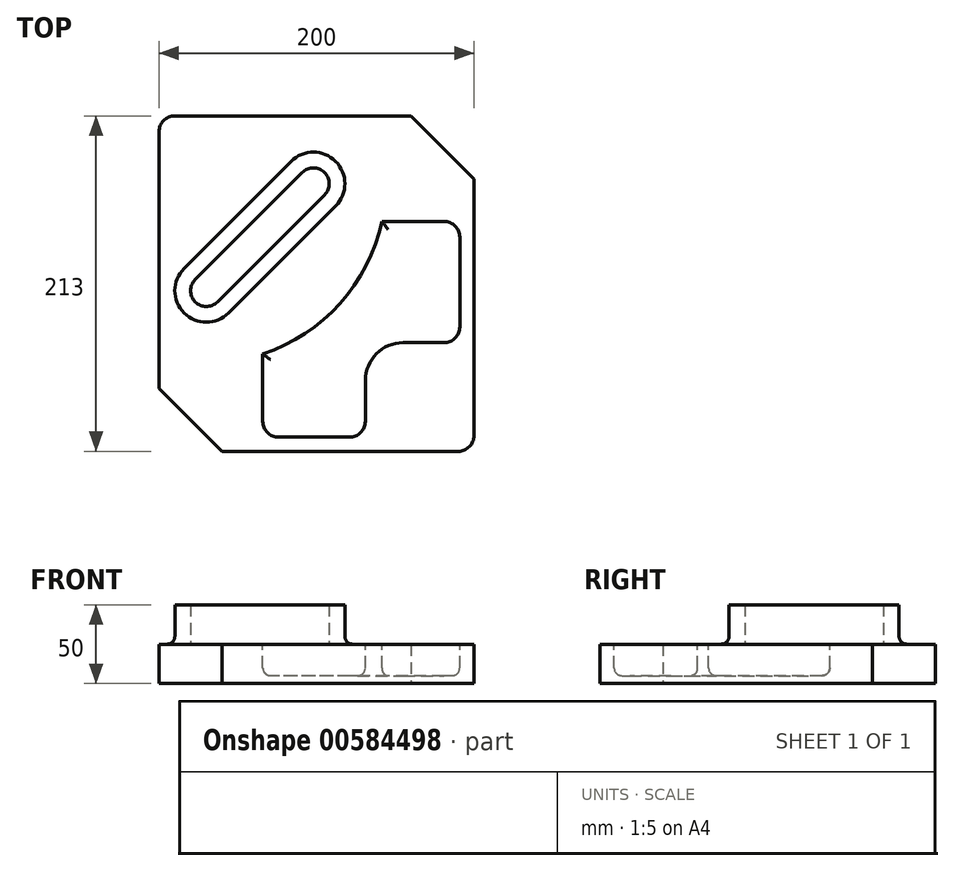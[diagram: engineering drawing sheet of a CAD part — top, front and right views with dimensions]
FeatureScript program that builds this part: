
annotation { "Feature Type Name" : "Feature", "Feature Type Description" : "" }
export const myFeature = defineFeature(function(context is Context, id is Id, definition is map)
    precondition{}
    {
        {
            var Q0;
            Q0=qCreatedBy(makeId("Top.planeOp"),FACE);
            var sketch = newSketch(context, id + "F0", { "sketchPlane" : qUnion([Q0])});
            skLineSegment(sketch, "E0.bottom", {"start": v(-60, -106.5) * mm, "end": v(100, -106.5) * mm});
            skLineSegment(sketch, "E0.top", {"start": v(-100, 106.5) * mm, "end": v(60, 106.5) * mm});
            skLineSegment(sketch, "E0.left", {"start": v(-100, -66.5) * mm, "end": v(-100, 106.5) * mm});
            skLineSegment(sketch, "E0.right", {"start": v(100, -106.5) * mm, "end": v(100, 66.5) * mm});
            skPoint(sketch, "E0.middle", {"position": v(0, 0) * mm});
            skLineSegment(sketch, "E1", {"start": v(60, 106.5) * mm, "end": v(100, 66.5) * mm});
            skLineSegment(sketch, "E2", {"start": v(-100, -66.5) * mm, "end": v(-60, -106.5) * mm});
            skPoint(sketch, "E3.orphan", {"position": v(100, 106.5) * mm});
            skPoint(sketch, "E4.orphan", {"position": v(-100, -106.5) * mm});
            skSolve(sketch);
        }
        {
            var Q0;
            Q0=makeQuery(id+"F0.imprint","IMPRINT",FACE,{"disambiguationData":[TD([[makeQuery(id+"F0.imprint","IMPRINT",EDGE,{"derivedFrom":sQuery(id+"F0.wireOp",EDGE,"E0.top")}),-1.0]])]});
            extrude(context, id + "F1", {"entities" : qUnion([Q0]), "depth" : 25 * mm, "offsetDistance" : 25 * mm});
        }
        {
            var Q0;
            Q0=makeQuery(id+"F1.opExtrude","CAP_FACE",FACE,{"disambiguationData":[OSD([sQuery(id+"F0.wireOp",EDGE,"E0.top"),sQuery(id+"F0.wireOp",EDGE,"E0.left"),sQuery(id+"F0.wireOp",EDGE,"E0.right"),sQuery(id+"F0.wireOp",EDGE,"E0.bottom"),sQuery(id+"F0.wireOp",EDGE,"E1"),sQuery(id+"F0.wireOp",EDGE,"E2")])],"isStart":true});
            cPlane(context, id + "F2", {"entities" : qUnion([Q0]), "cplaneType" : CPlaneType.OFFSET, "offset" : 25 * mm, "oppositeDirection" : true, "width" : 150 * mm, "height" : 150 * mm});
        }
        {
            var Q0;
            Q0=qCreatedBy(id+"F2.planeOp",FACE);
            var sketch = newSketch(context, id + "F3", { "sketchPlane" : qUnion([Q0])});
            skLineSegment(sketch, "E5", {"start": v(55, 37.5) * mm, "end": v(81, 37.5) * mm});
            skLineSegment(sketch, "E6", {"start": v(91, 27.5) * mm, "end": v(91, -29.5) * mm});
            skLineSegment(sketch, "E7", {"start": v(81, -39.5) * mm, "end": v(41.47, -39.5) * mm});
            skPoint(sketch, "E8.visualSharp", {"position": v(91, -39.5) * mm});
            skArc(sketch, "E8.filletArc", {"start": v(81, -39.5) * mm, "mid": v(88.07, -36.57) * mm, "end": v(91, -29.5) * mm});
            skPoint(sketch, "E9.visualSharp", {"position": v(91, 37.5) * mm});
            skArc(sketch, "E9.filletArc", {"start": v(91, 27.5) * mm, "mid": v(88.07, 34.57) * mm, "end": v(81, 37.5) * mm});
            skLineSegment(sketch, "E10", {"start": v(31, 61.5) * mm, "end": v(31, 87.5) * mm});
            skLineSegment(sketch, "E11", {"start": v(21, 97.5) * mm, "end": v(-24.13, 97.5) * mm});
            skLineSegment(sketch, "E12", {"start": v(-34.13, 87.5) * mm, "end": v(-34.13, 44.72) * mm});
            skPoint(sketch, "E13.visualSharp", {"position": v(31, 37.5) * mm});
            skArc(sketch, "E13.filletArc", {"start": v(31, 61.5) * mm, "mid": v(38.03, 44.53) * mm, "end": v(55, 37.5) * mm});
            skPoint(sketch, "E14.visualSharp", {"position": v(-34.13, 97.5) * mm});
            skArc(sketch, "E14.filletArc", {"start": v(-24.13, 97.5) * mm, "mid": v(-31.2, 94.57) * mm, "end": v(-34.13, 87.5) * mm});
            skPoint(sketch, "E15.visualSharp", {"position": v(31, 97.5) * mm});
            skArc(sketch, "E15.filletArc", {"start": v(31, 87.5) * mm, "mid": v(28.07, 94.57) * mm, "end": v(21, 97.5) * mm});
            skArc(sketch, "E16", {"start": v(41.47, -39.5) * mm, "mid": v(14.86, 12.66) * mm, "end": v(-34.13, 44.72) * mm});
            skSolve(sketch);
        }
        {
            var Q0;
            Q0=makeQuery(id+"F3.imprint","IMPRINT",FACE,{"disambiguationData":[TD([[makeQuery(id+"F3.imprint","IMPRINT",EDGE,{"derivedFrom":sQuery(id+"F3.wireOp",EDGE,"E5")}),-1.0]])]});
            extrude(context, id + "F4", {"entities" : qUnion([Q0]), "operationType" : NewBodyOperationType.REMOVE, "depth" : 20 * mm, "offsetDistance" : 25 * mm});
        }
        {
            var Q0;
            Q0=makeQuery(id+"F1.opExtrude","CAP_FACE",FACE,{"disambiguationData":[OSD([sQuery(id+"F0.wireOp",EDGE,"E0.top"),sQuery(id+"F0.wireOp",EDGE,"E0.left"),sQuery(id+"F0.wireOp",EDGE,"E0.right"),sQuery(id+"F0.wireOp",EDGE,"E0.bottom"),sQuery(id+"F0.wireOp",EDGE,"E1"),sQuery(id+"F0.wireOp",EDGE,"E2")])],"isStart":false});
            var sketch = newSketch(context, id + "F5", { "sketchPlane" : qUnion([Q0])});
            skArc(sketch, "E17", {"start": v(5.07, 56.43) * mm, "mid": v(5.07, 70.57) * mm, "end": v(-9.07, 70.57) * mm});
            skArc(sketch, "E18", {"start": v(-77.07, 2.57) * mm, "mid": v(-77.07, -11.57) * mm, "end": v(-62.93, -11.57) * mm});
            skLineSegment(sketch, "E19", {"start": v(-77.07, 2.57) * mm, "end": v(-9.07, 70.57) * mm});
            skLineSegment(sketch, "E20", {"start": v(-62.93, -11.57) * mm, "end": v(5.07, 56.43) * mm});
            skArc(sketch, "E21", {"start": v(-84.14, 9.64) * mm, "mid": v(-84.14, -18.64) * mm, "end": v(-55.86, -18.64) * mm});
            skArc(sketch, "E22", {"start": v(12.14, 49.36) * mm, "mid": v(12.14, 77.64) * mm, "end": v(-16.14, 77.64) * mm});
            skLineSegment(sketch, "E23", {"start": v(-84.14, 9.64) * mm, "end": v(-16.14, 77.64) * mm});
            skLineSegment(sketch, "E24", {"start": v(-55.86, -18.64) * mm, "end": v(12.14, 49.36) * mm});
            skSolve(sketch);
        }
        {
            var Q0;
            Q0=makeQuery(id+"F5.imprint","IMPRINT",FACE,{"disambiguationData":[TD([[makeQuery(id+"F5.imprint","IMPRINT",EDGE,{"derivedFrom":sQuery(id+"F5.wireOp",EDGE,"E17")}),-1.0]])]});
            extrude(context, id + "F6", {"entities" : qUnion([Q0]), "operationType" : NewBodyOperationType.ADD, "depth" : 25 * mm, "offsetDistance" : 25 * mm});
        }
        {
            var Q0;
            Q0=makeQuery(id+"F1.opExtrude","SWEPT_EDGE",EDGE,{"disambiguationData":[OSD([sQuery(id+"F0.wireOp",EDGE,"E0.right"),sQuery(id+"F0.wireOp",EDGE,"E0.bottom")])]});
            var Q1;
            Q1=makeQuery(id+"F1.opExtrude","SWEPT_EDGE",EDGE,{"disambiguationData":[OSD([sQuery(id+"F0.wireOp",EDGE,"E0.top"),sQuery(id+"F0.wireOp",EDGE,"E0.left")])]});
            fillet(context, id + "F7", {"entities" : qUnion([Q0, Q1]), "radius" : 10 * mm, "tangentPropagation" : true, "allowEdgeOverflow" : false});
        }
        {
            var Q0;
            Q0=makeQuery(id+"F4.boolean.opBoolean","COPY",EDGE,{"derivedFrom":makeQuery(id+"F4.opExtrude","CAP_EDGE",EDGE,{"disambiguationData":[OSD([sQuery(id+"F3.wireOp",EDGE,"E7")])],"isStart":false})});
            var Q1;
            Q1=makeQuery(id+"F4.boolean.opBoolean","COPY",EDGE,{"derivedFrom":makeQuery(id+"F4.opExtrude","CAP_EDGE",EDGE,{"disambiguationData":[OSD([sQuery(id+"F3.wireOp",EDGE,"E16")])],"isStart":false})});
            var Q2;
            Q2=makeQuery(id+"F4.boolean.opBoolean","COPY",EDGE,{"derivedFrom":makeQuery(id+"F4.opExtrude","CAP_EDGE",EDGE,{"disambiguationData":[OSD([sQuery(id+"F3.wireOp",EDGE,"E12")])],"isStart":false})});
            var Q3;
            Q3=makeQuery(id+"F4.boolean.opBoolean","COPY",EDGE,{"derivedFrom":makeQuery(id+"F4.opExtrude","CAP_EDGE",EDGE,{"disambiguationData":[OSD([sQuery(id+"F3.wireOp",EDGE,"E6")])],"isStart":false})});
            var Q4;
            Q4=makeQuery(id+"F6.opExtrude","CAP_EDGE",EDGE,{"disambiguationData":[OSD([sQuery(id+"F5.wireOp",EDGE,"E24")])],"isStart":true});
            var Q5;
            Q5=makeQuery(id+"F4.boolean.opBoolean","COPY",EDGE,{"derivedFrom":makeQuery(id+"F4.opExtrude","CAP_EDGE",EDGE,{"disambiguationData":[OSD([sQuery(id+"F3.wireOp",EDGE,"E16")])],"isStart":true})});
            var Q6;
            Q6=makeQuery(id+"F4.boolean.opBoolean","COPY",EDGE,{"derivedFrom":makeQuery(id+"F4.opExtrude","CAP_EDGE",EDGE,{"disambiguationData":[OSD([sQuery(id+"F3.wireOp",EDGE,"E7")])],"isStart":true})});
            fillet(context, id + "F8", {"entities" : qUnion([Q0, Q1, Q2, Q3, Q4, Q5, Q6]), "radius" : 5 * mm, "tangentPropagation" : true, "allowEdgeOverflow" : false});
        }
    });
